# Revit family: QF_MOFFAT_BLUESEAL_CE_G47
name_source: partatom
category: Specialty Equipment
revit_build: Autodesk Revit Architecture 2012 (Build: 20110309_2315(x64)
units: mm (PartAtom-declared; Revit-internal decimal feet)

## types (1)
- QF_MOFFAT_BLUESEAL_CE_G47
    Cold Water Connection Height = 0 mm  [stored 0 ft]
    Cold Water Maximum Pressure = 0.00 psi
    Cold Water Minimum Pressure = 0.00 psi
    Cold Water Size = 1"
    Description = 450MM GAS PASTA COOKER SINGLE PAN
    Gas Connection Height = 0 mm  [stored 0 ft]
    Gas Input = 46000.0 Btu/h
    Gas KW = 13.5
    Gas Size = 1"
    Indirect Waste Connection Height = 0 mm  [stored 0 ft]
    Indirect Waste Size = 1"
    Manufacturer = MOFFAT BLUESEAL
    Model = G47
    URL = www.moffat.com
    URL Cutsheet = www.moffat.com
    Weight in Pounds = 182

note: [stored X ft] marks values corroborated as IEEE doubles in the binary element streams (Revit-internal decimal feet)

## geometry (parser evidence)
native form markers: Blend x10, Sweep x5
no freeform markers — native parametric forms only
